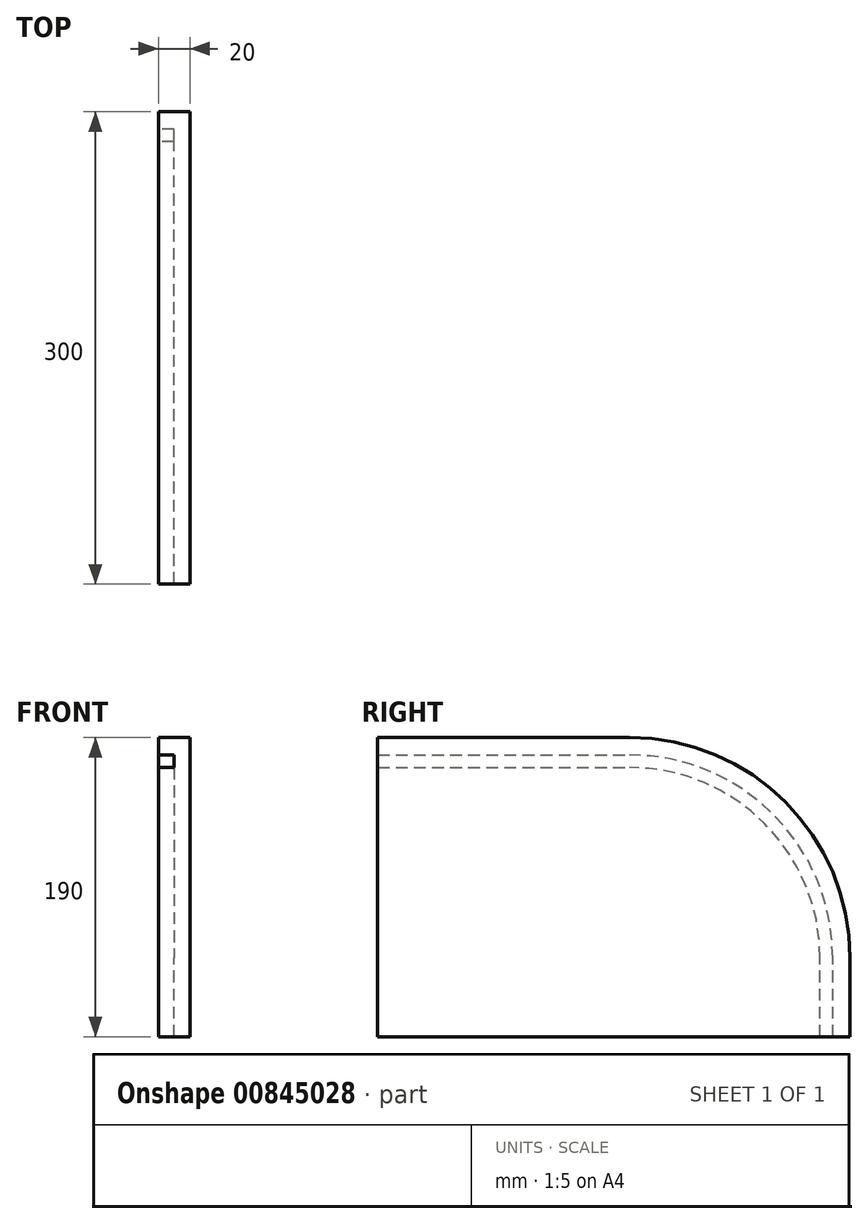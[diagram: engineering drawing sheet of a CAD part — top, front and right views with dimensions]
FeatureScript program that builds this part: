
annotation { "Feature Type Name" : "Feature", "Feature Type Description" : "" }
export const myFeature = defineFeature(function(context is Context, id is Id, definition is map)
    precondition{}
    {
        {
            var Q0;
            Q0=qCreatedBy(makeId("Right.planeOp"),FACE);
            var sketch = newSketch(context, id + "F0", { "sketchPlane" : qUnion([Q0])});
            skLineSegment(sketch, "E0.bottom", {"start": v(-150, 95) * mm, "end": v(150, 95) * mm});
            skLineSegment(sketch, "E0.top", {"start": v(-150, -95) * mm, "end": v(150, -95) * mm});
            skLineSegment(sketch, "E0.left", {"start": v(-150, 95) * mm, "end": v(-150, -95) * mm});
            skLineSegment(sketch, "E0.right", {"start": v(150, 95) * mm, "end": v(150, -95) * mm});
            skPoint(sketch, "E0.middle", {"position": v(0, 0) * mm});
            skSolve(sketch);
        }
        {
            var Q0;
            Q0=makeQuery(id+"F0.imprint","IMPRINT",FACE,{"disambiguationData":[TD([[makeQuery(id+"F0.imprint","IMPRINT",EDGE,{"derivedFrom":sQuery(id+"F0.wireOp",EDGE,"E0.bottom")}),-1.0]])]});
            extrude(context, id + "F1", {"entities" : qUnion([Q0]), "depth" : 20 * mm, "offsetDistance" : 25 * mm});
        }
        {
            var Q0;
            Q0=makeQuery(id+"F1.opExtrude","SWEPT_EDGE",EDGE,{"disambiguationData":[OSD([sQuery(id+"F0.wireOp",EDGE,"E0.bottom"),sQuery(id+"F0.wireOp",EDGE,"E0.right")])]});
            fillet(context, id + "F2", {"entities" : qUnion([Q0]), "radius" : 140 * mm, "tangentPropagation" : true, "allowEdgeOverflow" : false});
        }
        {
            var Q0;
            Q0=makeQuery(id+"F1.opExtrude","CAP_FACE",FACE,{"disambiguationData":[OSD([sQuery(id+"F0.wireOp",EDGE,"E0.bottom"),sQuery(id+"F0.wireOp",EDGE,"E0.top"),sQuery(id+"F0.wireOp",EDGE,"E0.left"),sQuery(id+"F0.wireOp",EDGE,"E0.right")])],"isStart":true});
            var sketch = newSketch(context, id + "F3", { "sketchPlane" : qUnion([Q0])});
            skPoint(sketch, "E1", {"position": v(-139, -95) * mm});
            skPoint(sketch, "E2", {"position": v(-131, -95) * mm});
            skLineSegment(sketch, "E3", {"start": v(-139, -95) * mm, "end": v(-139, -45) * mm});
            skLineSegment(sketch, "E4", {"start": v(-131, -95) * mm, "end": v(-131, -45) * mm});
            skPoint(sketch, "E5", {"position": v(150, 84) * mm});
            skPoint(sketch, "E6", {"position": v(150, 76) * mm});
            skLineSegment(sketch, "E7", {"start": v(150, 84) * mm, "end": v(-10, 84) * mm});
            skLineSegment(sketch, "E8", {"start": v(150, 76) * mm, "end": v(-10, 76) * mm});
            skArc(sketch, "E9", {"start": v(-10, 84) * mm, "mid": v(-101.22, 46.22) * mm, "end": v(-139, -45) * mm});
            skArc(sketch, "E10", {"start": v(-10, 76) * mm, "mid": v(-95.56, 40.56) * mm, "end": v(-131, -45) * mm});
            skSolve(sketch);
        }
        {
            var Q0;
            {var subQ4=sQuery(id+"F3.wireOp",EDGE,"E3");Q0=makeQuery(id+"F3.imprint","IMPRINT",FACE,{"disambiguationData":[TD([[makeQuery(id+"F3.imprint","IMPRINT",EDGE,{"derivedFrom":subQ4}),-1.0]])]});}
            extrude(context, id + "F4", {"entities" : qUnion([Q0]), "operationType" : NewBodyOperationType.REMOVE, "oppositeDirection" : true, "depth" : 10 * mm, "offsetDistance" : 25 * mm});
        }
    });
